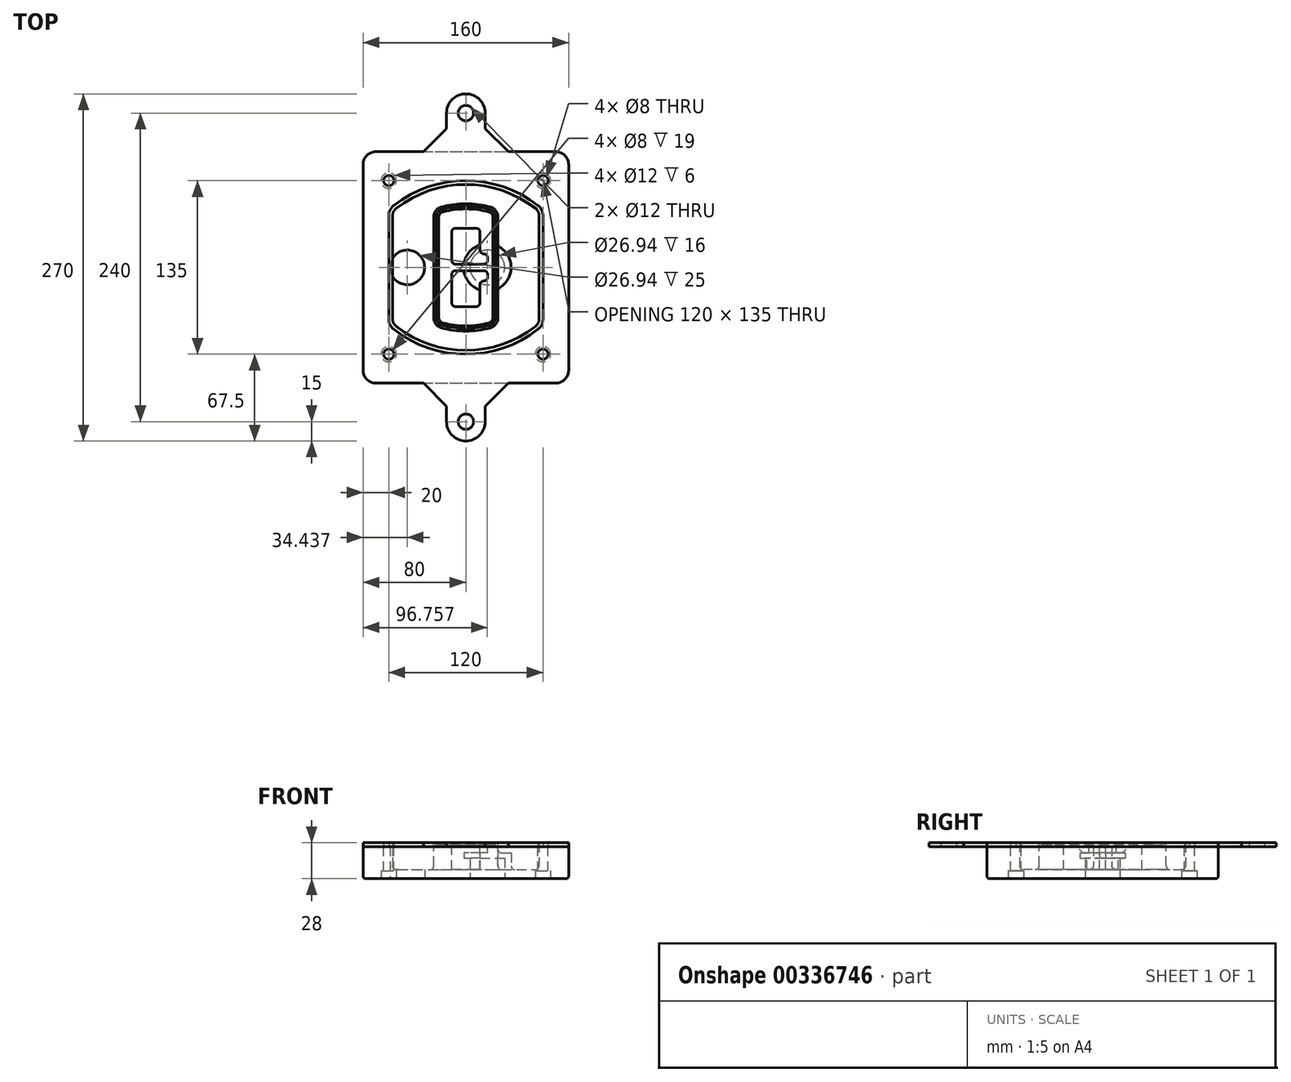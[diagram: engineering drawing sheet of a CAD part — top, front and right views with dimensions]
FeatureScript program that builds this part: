
annotation { "Feature Type Name" : "Feature", "Feature Type Description" : "" }
export const myFeature = defineFeature(function(context is Context, id is Id, definition is map)
    precondition{}
    {
        {
            var Q0;
            Q0=qCreatedBy(makeId("Top.planeOp"),FACE);
            var sketch = newSketch(context, id + "F0", { "sketchPlane" : qUnion([Q0])});
            skPoint(sketch, "E0.rect.middle", {"position": v(0, 0) * mm});
            skLineSegment(sketch, "E1.bottom", {"start": v(-70, -90) * mm, "end": v(70, -90) * mm});
            skLineSegment(sketch, "E1.top", {"start": v(-70, 90) * mm, "end": v(70, 90) * mm});
            skLineSegment(sketch, "E1.left", {"start": v(-80, -80) * mm, "end": v(-80, 80) * mm});
            skLineSegment(sketch, "E1.right", {"start": v(80, -80) * mm, "end": v(80, 80) * mm});
            skLineSegment(sketch, "E2", {"start": v(-80, 90) * mm, "end": v(80, -90) * mm, "construction": true});
            skLineSegment(sketch, "E3", {"start": v(80, 90) * mm, "end": v(-80, -90) * mm, "construction": true});
            skCircle(sketch, "E4", {"center": v(-60, 67.5) * mm, "radius": 4 * mm});
            skCircle(sketch, "E5", {"center": v(60, 67.5) * mm, "radius": 4 * mm});
            skCircle(sketch, "E6", {"center": v(60, -67.5) * mm, "radius": 4 * mm});
            skCircle(sketch, "E7", {"center": v(-60, -67.5) * mm, "radius": 4 * mm});
            skLineSegment(sketch, "E8", {"start": v(-60, 67.5) * mm, "end": v(60, 67.5) * mm, "construction": true});
            skLineSegment(sketch, "E9", {"start": v(60, 67.5) * mm, "end": v(60, -67.5) * mm, "construction": true});
            skLineSegment(sketch, "E10", {"start": v(60, -67.5) * mm, "end": v(-60, -67.5) * mm, "construction": true});
            skLineSegment(sketch, "E11", {"start": v(-60, -67.5) * mm, "end": v(-60, 67.5) * mm, "construction": true});
            skLineSegment(sketch, "E12", {"start": v(-60, 40.3) * mm, "end": v(-60, -40.3) * mm});
            skLineSegment(sketch, "E13", {"start": v(60, 40.3) * mm, "end": v(60, -40.3) * mm});
            skArc(sketch, "E14", {"start": v(56.15, 48.18) * mm, "mid": v(0, 67.5) * mm, "end": v(-56.15, 48.18) * mm});
            skArc(sketch, "E15", {"start": v(-56.15, -48.18) * mm, "mid": v(0, -67.5) * mm, "end": v(56.15, -48.18) * mm});
            skLineSegment(sketch, "E16", {"start": v(-60, 0) * mm, "end": v(60, 0) * mm, "construction": true});
            skPoint(sketch, "E17.visualSharp", {"position": v(-60, -45) * mm});
            skArc(sketch, "E17.filletArc", {"start": v(-60, -40.3) * mm, "mid": v(-58.99, -44.68) * mm, "end": v(-56.15, -48.18) * mm});
            skPoint(sketch, "E18.visualSharp", {"position": v(-60, 45) * mm});
            skArc(sketch, "E18.filletArc", {"start": v(-56.15, 48.18) * mm, "mid": v(-58.99, 44.68) * mm, "end": v(-60, 40.3) * mm});
            skPoint(sketch, "E19.visualSharp", {"position": v(60, 45) * mm});
            skArc(sketch, "E19.filletArc", {"start": v(60, 40.3) * mm, "mid": v(58.99, 44.68) * mm, "end": v(56.15, 48.18) * mm});
            skPoint(sketch, "E20.visualSharp", {"position": v(60, -45) * mm});
            skArc(sketch, "E20.filletArc", {"start": v(56.15, -48.18) * mm, "mid": v(58.99, -44.68) * mm, "end": v(60, -40.3) * mm});
            skPoint(sketch, "E21.visualSharp", {"position": v(-80, 90) * mm});
            skArc(sketch, "E21.filletArc", {"start": v(-70, 90) * mm, "mid": v(-77.07, 87.07) * mm, "end": v(-80, 80) * mm});
            skPoint(sketch, "E22.visualSharp", {"position": v(80, 90) * mm});
            skArc(sketch, "E22.filletArc", {"start": v(80, 80) * mm, "mid": v(77.07, 87.07) * mm, "end": v(70, 90) * mm});
            skPoint(sketch, "E23.visualSharp", {"position": v(80, -90) * mm});
            skArc(sketch, "E23.filletArc", {"start": v(70, -90) * mm, "mid": v(77.07, -87.07) * mm, "end": v(80, -80) * mm});
            skPoint(sketch, "E24.visualSharp", {"position": v(-80, -90) * mm});
            skArc(sketch, "E24.filletArc", {"start": v(-80, -80) * mm, "mid": v(-77.07, -87.07) * mm, "end": v(-70, -90) * mm});
            skArc(sketch, "E25.0", {"start": v(57, 40.3) * mm, "mid": v(56.3, 43.36) * mm, "end": v(54.3, 45.81) * mm});
            skLineSegment(sketch, "E25.1", {"start": v(57, 40.3) * mm, "end": v(57, -40.3) * mm});
            skArc(sketch, "E25.2", {"start": v(54.3, -45.81) * mm, "mid": v(56.3, -43.36) * mm, "end": v(57, -40.3) * mm});
            skArc(sketch, "E25.3", {"start": v(-54.3, -45.81) * mm, "mid": v(0, -64.5) * mm, "end": v(54.3, -45.81) * mm});
            skArc(sketch, "E25.4", {"start": v(-57, -40.3) * mm, "mid": v(-56.3, -43.36) * mm, "end": v(-54.3, -45.81) * mm});
            skArc(sketch, "E25.5", {"start": v(54.3, 45.81) * mm, "mid": v(0, 64.5) * mm, "end": v(-54.3, 45.81) * mm});
            skLineSegment(sketch, "E25.6", {"start": v(-57, 40.3) * mm, "end": v(-57, -40.3) * mm});
            skArc(sketch, "E25.7", {"start": v(-54.3, 45.81) * mm, "mid": v(-56.3, 43.36) * mm, "end": v(-57, 40.3) * mm});
            skArc(sketch, "E26.0", {"start": v(-58.62, 51.33) * mm, "mid": v(-62.58, 46.43) * mm, "end": v(-64, 40.3) * mm});
            skArc(sketch, "E26.1", {"start": v(58.62, 51.33) * mm, "mid": v(0, 71.5) * mm, "end": v(-58.62, 51.33) * mm});
            skArc(sketch, "E26.2", {"start": v(64, 40.3) * mm, "mid": v(62.58, 46.43) * mm, "end": v(58.62, 51.33) * mm});
            skLineSegment(sketch, "E26.3", {"start": v(64, 40.3) * mm, "end": v(64, -40.3) * mm});
            skArc(sketch, "E26.4", {"start": v(58.62, -51.33) * mm, "mid": v(62.58, -46.43) * mm, "end": v(64, -40.3) * mm});
            skLineSegment(sketch, "E26.5", {"start": v(-64, 40.3) * mm, "end": v(-64, -40.3) * mm});
            skArc(sketch, "E26.6", {"start": v(-58.62, -51.33) * mm, "mid": v(0, -71.5) * mm, "end": v(58.62, -51.33) * mm});
            skArc(sketch, "E26.7", {"start": v(-64, -40.3) * mm, "mid": v(-62.58, -46.43) * mm, "end": v(-58.62, -51.33) * mm});
            skSolve(sketch);
        }
        {
            var Q0;
            Q0=makeQuery(id+"F0.imprint","IMPRINT",FACE,{"disambiguationData":[TD([[makeQuery(id+"F0.imprint","IMPRINT",EDGE,{"derivedFrom":sQuery(id+"F0.wireOp",EDGE,"E1.bottom")}),1.0]])]});
            var Q1;
            Q1=makeQuery(id+"F0.imprint","IMPRINT",FACE,{"disambiguationData":[TD([[makeQuery(id+"F0.imprint","IMPRINT",EDGE,{"derivedFrom":sQuery(id+"F0.wireOp",EDGE,"E12")}),1.0]])]});
            var Q2;
            Q2=makeQuery(id+"F0.imprint","IMPRINT",FACE,{"disambiguationData":[TD([[makeQuery(id+"F0.imprint","IMPRINT",EDGE,{"derivedFrom":sQuery(id+"F0.wireOp",EDGE,"E25.0")}),1.0]])]});
            var Q3;
            Q3=makeQuery(id+"F0.imprint","IMPRINT",FACE,{"disambiguationData":[TD([[makeQuery(id+"F0.imprint","IMPRINT",EDGE,{"derivedFrom":sQuery(id+"F0.wireOp",EDGE,"E12")}),-1.0]])]});
            extrude(context, id + "F1", {"entities" : qUnion([Q0, Q1, Q2, Q3]), "oppositeDirection" : true, "depth" : 25 * mm});
        }
        {
            var Q0;
            Q0=makeQuery(id+"F0.imprint","IMPRINT",FACE,{"disambiguationData":[TD([[makeQuery(id+"F0.imprint","IMPRINT",EDGE,{"derivedFrom":sQuery(id+"F0.wireOp",EDGE,"E12")}),1.0]])]});
            extrude(context, id + "F2", {"entities" : qUnion([Q0]), "operationType" : NewBodyOperationType.ADD, "depth" : 3 * mm});
        }
        {
            var Q0;
            Q0=makeQuery(id+"F0.imprint","IMPRINT",FACE,{"disambiguationData":[TD([[makeQuery(id+"F0.imprint","IMPRINT",EDGE,{"derivedFrom":sQuery(id+"F0.wireOp",EDGE,"E25.0")}),1.0]])]});
            extrude(context, id + "F3", {"entities" : qUnion([Q0]), "operationType" : NewBodyOperationType.REMOVE, "oppositeDirection" : true, "depth" : 18 * mm});
        }
        {
            var Q0;
            Q0=makeQuery(id+"F2.opExtrude","CAP_FACE",FACE,{"disambiguationData":[OSD([sQuery(id+"F0.wireOp",EDGE,"E12"),sQuery(id+"F0.wireOp",EDGE,"E13"),sQuery(id+"F0.wireOp",EDGE,"E14"),sQuery(id+"F0.wireOp",EDGE,"E15"),sQuery(id+"F0.wireOp",EDGE,"E17.filletArc"),sQuery(id+"F0.wireOp",EDGE,"E18.filletArc"),sQuery(id+"F0.wireOp",EDGE,"E19.filletArc"),sQuery(id+"F0.wireOp",EDGE,"E20.filletArc"),sQuery(id+"F0.wireOp",EDGE,"E25.0"),sQuery(id+"F0.wireOp",EDGE,"E25.1"),sQuery(id+"F0.wireOp",EDGE,"E25.2"),sQuery(id+"F0.wireOp",EDGE,"E25.3"),sQuery(id+"F0.wireOp",EDGE,"E25.4"),sQuery(id+"F0.wireOp",EDGE,"E25.5"),sQuery(id+"F0.wireOp",EDGE,"E25.6"),sQuery(id+"F0.wireOp",EDGE,"E25.7")])],"isStart":false});
            var sketch = newSketch(context, id + "F4", { "sketchPlane" : qUnion([Q0])});
            skArc(sketch, "E27.0", {"start": v(-19.08, -46.97) * mm, "mid": v(0, -49.5) * mm, "end": v(19.08, -46.97) * mm});
            skArc(sketch, "E28.0", {"start": v(19.08, 46.97) * mm, "mid": v(0, 49.5) * mm, "end": v(-19.08, 46.97) * mm});
            skLineSegment(sketch, "E29", {"start": v(-25, 39.25) * mm, "end": v(-25, -39.25) * mm});
            skLineSegment(sketch, "E30", {"start": v(25, 39.25) * mm, "end": v(25, -39.25) * mm});
            skLineSegment(sketch, "E31", {"start": v(-25, 45.1) * mm, "end": v(25, 45.1) * mm, "construction": true});
            skLineSegment(sketch, "E32", {"start": v(-25, -45.1) * mm, "end": v(25, -45.1) * mm, "construction": true});
            skPoint(sketch, "E33.visualSharp", {"position": v(-25, 45.1) * mm});
            skArc(sketch, "E33.filletArc", {"start": v(-19.08, 46.97) * mm, "mid": v(-23.35, 44.11) * mm, "end": v(-25, 39.25) * mm});
            skPoint(sketch, "E34.visualSharp", {"position": v(25, 45.1) * mm});
            skArc(sketch, "E34.filletArc", {"start": v(25, 39.25) * mm, "mid": v(23.35, 44.11) * mm, "end": v(19.08, 46.97) * mm});
            skPoint(sketch, "E35.visualSharp", {"position": v(25, -45.1) * mm});
            skArc(sketch, "E35.filletArc", {"start": v(19.08, -46.97) * mm, "mid": v(23.35, -44.11) * mm, "end": v(25, -39.25) * mm});
            skPoint(sketch, "E36.visualSharp", {"position": v(-25, -45.1) * mm});
            skArc(sketch, "E36.filletArc", {"start": v(-25, -39.25) * mm, "mid": v(-23.35, -44.11) * mm, "end": v(-19.08, -46.97) * mm});
            skArc(sketch, "E37.0", {"start": v(54.3, 45.81) * mm, "mid": v(0, 64.5) * mm, "end": v(-54.3, 45.81) * mm});
            skArc(sketch, "E37.1", {"start": v(-54.3, 45.81) * mm, "mid": v(-56.3, 43.36) * mm, "end": v(-57, 40.3) * mm});
            skLineSegment(sketch, "E37.2", {"start": v(-57, 40.3) * mm, "end": v(-57, -40.3) * mm});
            skArc(sketch, "E37.3", {"start": v(-57, -40.3) * mm, "mid": v(-56.3, -43.36) * mm, "end": v(-54.3, -45.81) * mm});
            skArc(sketch, "E37.4", {"start": v(-54.3, -45.81) * mm, "mid": v(0, -64.5) * mm, "end": v(54.3, -45.81) * mm});
            skArc(sketch, "E37.5", {"start": v(54.3, -45.81) * mm, "mid": v(56.3, -43.36) * mm, "end": v(57, -40.3) * mm});
            skLineSegment(sketch, "E37.6", {"start": v(57, 40.3) * mm, "end": v(57, -40.3) * mm});
            skArc(sketch, "E37.7", {"start": v(57, 40.3) * mm, "mid": v(56.3, 43.36) * mm, "end": v(54.3, 45.81) * mm});
            skLineSegment(sketch, "E38.0", {"start": v(23, 39.25) * mm, "end": v(23, -39.25) * mm});
            skArc(sketch, "E38.1", {"start": v(18.56, -45.04) * mm, "mid": v(21.76, -42.9) * mm, "end": v(23, -39.25) * mm});
            skArc(sketch, "E38.2", {"start": v(-18.56, -45.04) * mm, "mid": v(0, -47.5) * mm, "end": v(18.56, -45.04) * mm});
            skArc(sketch, "E38.3", {"start": v(-23, -39.25) * mm, "mid": v(-21.76, -42.9) * mm, "end": v(-18.56, -45.04) * mm});
            skLineSegment(sketch, "E38.4", {"start": v(-23, 39.25) * mm, "end": v(-23, -39.25) * mm});
            skArc(sketch, "E38.5", {"start": v(23, 39.25) * mm, "mid": v(21.76, 42.9) * mm, "end": v(18.56, 45.04) * mm});
            skArc(sketch, "E38.6", {"start": v(-18.56, 45.04) * mm, "mid": v(-21.76, 42.9) * mm, "end": v(-23, 39.25) * mm});
            skArc(sketch, "E38.7", {"start": v(18.56, 45.04) * mm, "mid": v(0, 47.5) * mm, "end": v(-18.56, 45.04) * mm});
            skArc(sketch, "E39.0", {"start": v(21, 39.25) * mm, "mid": v(20.18, 41.68) * mm, "end": v(18.04, 43.1) * mm});
            skLineSegment(sketch, "E39.1", {"start": v(21, 39.25) * mm, "end": v(21, -39.25) * mm});
            skArc(sketch, "E39.2", {"start": v(18.04, -43.1) * mm, "mid": v(20.18, -41.68) * mm, "end": v(21, -39.25) * mm});
            skArc(sketch, "E39.3", {"start": v(-18.04, -43.1) * mm, "mid": v(0, -45.5) * mm, "end": v(18.04, -43.1) * mm});
            skArc(sketch, "E39.4", {"start": v(-21, -39.25) * mm, "mid": v(-20.18, -41.68) * mm, "end": v(-18.04, -43.1) * mm});
            skArc(sketch, "E39.5", {"start": v(18.04, 43.1) * mm, "mid": v(0, 45.5) * mm, "end": v(-18.04, 43.1) * mm});
            skLineSegment(sketch, "E39.6", {"start": v(-21, 39.25) * mm, "end": v(-21, -39.25) * mm});
            skArc(sketch, "E39.7", {"start": v(-18.04, 43.1) * mm, "mid": v(-20.18, 41.68) * mm, "end": v(-21, 39.25) * mm});
            skLineSegment(sketch, "E40", {"start": v(-25, 0) * mm, "end": v(25, 0) * mm, "construction": true});
            skLineSegment(sketch, "E41", {"start": v(-11, 5.5) * mm, "end": v(-11, 27.5) * mm});
            skLineSegment(sketch, "E42", {"start": v(-8, 30.5) * mm, "end": v(8, 30.5) * mm});
            skLineSegment(sketch, "E43", {"start": v(11, 27.5) * mm, "end": v(11, 13.5) * mm});
            skLineSegment(sketch, "E44", {"start": v(14, 10.5) * mm, "end": v(14, 10.5) * mm});
            skLineSegment(sketch, "E45", {"start": v(17, 7.5) * mm, "end": v(17, 5.5) * mm});
            skLineSegment(sketch, "E46", {"start": v(14, 2.5) * mm, "end": v(-8, 2.5) * mm});
            skPoint(sketch, "E47.visualSharp", {"position": v(-11, 30.5) * mm});
            skArc(sketch, "E47.filletArc", {"start": v(-8, 30.5) * mm, "mid": v(-10.12, 29.62) * mm, "end": v(-11, 27.5) * mm});
            skPoint(sketch, "E48.visualSharp", {"position": v(11, 30.5) * mm});
            skArc(sketch, "E48.filletArc", {"start": v(11, 27.5) * mm, "mid": v(10.12, 29.62) * mm, "end": v(8, 30.5) * mm});
            skPoint(sketch, "E49.visualSharp", {"position": v(11, 10.5) * mm});
            skArc(sketch, "E49.filletArc", {"start": v(11, 13.5) * mm, "mid": v(11.88, 11.38) * mm, "end": v(14, 10.5) * mm});
            skPoint(sketch, "E50.visualSharp", {"position": v(17, 10.5) * mm});
            skArc(sketch, "E50.filletArc", {"start": v(17, 7.5) * mm, "mid": v(16.12, 9.62) * mm, "end": v(14, 10.5) * mm});
            skPoint(sketch, "E51.visualSharp", {"position": v(17, 2.5) * mm});
            skArc(sketch, "E51.filletArc", {"start": v(14, 2.5) * mm, "mid": v(16.12, 3.38) * mm, "end": v(17, 5.5) * mm});
            skPoint(sketch, "E52.visualSharp", {"position": v(-11, 2.5) * mm});
            skArc(sketch, "E52.filletArc", {"start": v(-11, 5.5) * mm, "mid": v(-10.12, 3.38) * mm, "end": v(-8, 2.5) * mm});
            skLineSegment(sketch, "E53.0.MirrorCS", {"start": v(14, -2.5) * mm, "end": v(-8, -2.5) * mm});
            skArc(sketch, "E54.0.MirrorCS", {"start": v(-11, -5.5) * mm, "mid": v(-10.12, -3.38) * mm, "end": v(-8, -2.5) * mm});
            skLineSegment(sketch, "E55.0.MirrorCS", {"start": v(-11, -5.5) * mm, "end": v(-11, -27.5) * mm});
            skArc(sketch, "E56.0.MirrorCS", {"start": v(-8, -30.5) * mm, "mid": v(-10.12, -29.62) * mm, "end": v(-11, -27.5) * mm});
            skLineSegment(sketch, "E57.0.MirrorCS", {"start": v(-8, -30.5) * mm, "end": v(8, -30.5) * mm});
            skArc(sketch, "E58.0.MirrorCS", {"start": v(11, -27.5) * mm, "mid": v(10.12, -29.62) * mm, "end": v(8, -30.5) * mm});
            skLineSegment(sketch, "E59.0.MirrorCS", {"start": v(11, -27.5) * mm, "end": v(11, -13.5) * mm});
            skArc(sketch, "E60.0.MirrorCS", {"start": v(11, -13.5) * mm, "mid": v(11.88, -11.38) * mm, "end": v(14, -10.5) * mm});
            skArc(sketch, "E61.0.MirrorCS", {"start": v(17, -7.5) * mm, "mid": v(16.12, -9.62) * mm, "end": v(14, -10.5) * mm});
            skLineSegment(sketch, "E62.0.MirrorCS", {"start": v(17, -7.5) * mm, "end": v(17, -5.5) * mm});
            skArc(sketch, "E63.0.MirrorCS", {"start": v(14, -2.5) * mm, "mid": v(16.12, -3.38) * mm, "end": v(17, -5.5) * mm});
            skSolve(sketch);
        }
        {
            var Q0;
            Q0=makeQuery(id+"F4.imprint","IMPRINT",FACE,{"disambiguationData":[TD([[makeQuery(id+"F4.imprint","IMPRINT",EDGE,{"derivedFrom":sQuery(id+"F4.wireOp",EDGE,"E27.0")}),1.0]])]});
            var Q1;
            Q1=makeQuery(id+"F4.imprint","IMPRINT",FACE,{"disambiguationData":[TD([[makeQuery(id+"F4.imprint","IMPRINT",EDGE,{"derivedFrom":sQuery(id+"F4.wireOp",EDGE,"E38.0")}),-1.0]])]});
            var Q2;
            Q2=makeQuery(id+"F4.imprint","IMPRINT",FACE,{"disambiguationData":[TD([[makeQuery(id+"F4.imprint","IMPRINT",EDGE,{"derivedFrom":sQuery(id+"F4.wireOp",EDGE,"E39.0")}),1.0]])]});
            extrude(context, id + "F5", {"entities" : qUnion([Q0, Q1, Q2]), "operationType" : NewBodyOperationType.ADD, "endBound" : BoundingType.UP_TO_NEXT, "oppositeDirection" : true, "depth" : 25 * mm});
        }
        {
            var Q0;
            Q0=makeQuery(id+"F4.imprint","IMPRINT",FACE,{"disambiguationData":[TD([[makeQuery(id+"F4.imprint","IMPRINT",EDGE,{"derivedFrom":sQuery(id+"F4.wireOp",EDGE,"E38.0")}),-1.0]])]});
            extrude(context, id + "F6", {"entities" : qUnion([Q0]), "operationType" : NewBodyOperationType.REMOVE, "oppositeDirection" : true, "depth" : 2 * mm});
        }
        {
            var Q0;
            Q0=makeQuery(id+"F1.opExtrude","CAP_FACE",FACE,{"disambiguationData":[OSD([sQuery(id+"F0.wireOp",EDGE,"E1.bottom"),sQuery(id+"F0.wireOp",EDGE,"E1.top"),sQuery(id+"F0.wireOp",EDGE,"E1.left"),sQuery(id+"F0.wireOp",EDGE,"E1.right"),sQuery(id+"F0.wireOp",EDGE,"E4"),sQuery(id+"F0.wireOp",EDGE,"E5"),sQuery(id+"F0.wireOp",EDGE,"E6"),sQuery(id+"F0.wireOp",EDGE,"E7"),sQuery(id+"F0.wireOp",EDGE,"E21.filletArc"),sQuery(id+"F0.wireOp",EDGE,"E22.filletArc"),sQuery(id+"F0.wireOp",EDGE,"E23.filletArc"),sQuery(id+"F0.wireOp",EDGE,"E24.filletArc")])],"isStart":false});
            var sketch = newSketch(context, id + "F7", { "sketchPlane" : qUnion([Q0])});
            skCircle(sketch, "E64", {"center": v(16.76, 0) * mm, "radius": 13.47 * mm});
            skCircle(sketch, "E65", {"center": v(-45.56, 0) * mm, "radius": 13.47 * mm});
            skLineSegment(sketch, "E66", {"start": v(80, 0) * mm, "end": v(-80, 0) * mm});
            skCircle(sketch, "E67", {"center": v(16.76, 0) * mm, "radius": 18.47 * mm});
            skCircle(sketch, "E68", {"center": v(60, -67.5) * mm, "radius": 6 * mm});
            skCircle(sketch, "E69", {"center": v(-60, -67.5) * mm, "radius": 6 * mm});
            skCircle(sketch, "E70", {"center": v(-60, 67.5) * mm, "radius": 6 * mm});
            skCircle(sketch, "E71", {"center": v(60, 67.5) * mm, "radius": 6 * mm});
            skSolve(sketch);
        }
        {
            var Q0;
            {var subQ1=sQuery(id+"F7.wireOp",EDGE,"E66");var subQ4=sQuery(id+"F7.wireOp",EDGE,"E64");var subQ6=makeQuery(id+"F7.imprint","INTERSECT",VERTEX,{"disambiguationData":[OD(0.0)],"derivedFrom":[subQ4,subQ1]});Q0=makeQuery(id+"F7.imprint","IMPRINT",FACE,{"disambiguationData":[TD([[makeQuery(id+"F7.imprint","IMPRINT",EDGE,{"disambiguationData":[TD([[subQ6,-1.0]])],"derivedFrom":subQ4}),-1.0]])]});}
            var Q1;
            {var subQ0=sQuery(id+"F7.wireOp",EDGE,"E66");var subQ1=sQuery(id+"F7.wireOp",EDGE,"E64");var subQ3=makeQuery(id+"F7.imprint","INTERSECT",VERTEX,{"disambiguationData":[OD(0.0)],"derivedFrom":[subQ1,subQ0]});Q1=makeQuery(id+"F7.imprint","IMPRINT",FACE,{"disambiguationData":[TD([[makeQuery(id+"F7.imprint","IMPRINT",EDGE,{"disambiguationData":[TD([[subQ3,-1.0]])],"derivedFrom":subQ1}),1.0]])]});}
            var Q2;
            {var subQ0=sQuery(id+"F7.wireOp",EDGE,"E66");var subQ1=sQuery(id+"F7.wireOp",EDGE,"E64");var subQ3=makeQuery(id+"F7.imprint","INTERSECT",VERTEX,{"disambiguationData":[OD(0.0)],"derivedFrom":[subQ1,subQ0]});Q2=makeQuery(id+"F7.imprint","IMPRINT",FACE,{"disambiguationData":[TD([[makeQuery(id+"F7.imprint","IMPRINT",EDGE,{"disambiguationData":[TD([[subQ3,1.0]])],"derivedFrom":subQ1}),1.0]])]});}
            var Q3;
            {var subQ1=sQuery(id+"F7.wireOp",EDGE,"E66");var subQ4=sQuery(id+"F7.wireOp",EDGE,"E64");var subQ6=makeQuery(id+"F7.imprint","INTERSECT",VERTEX,{"disambiguationData":[OD(0.0)],"derivedFrom":[subQ4,subQ1]});Q3=makeQuery(id+"F7.imprint","IMPRINT",FACE,{"disambiguationData":[TD([[makeQuery(id+"F7.imprint","IMPRINT",EDGE,{"disambiguationData":[TD([[subQ6,1.0]])],"derivedFrom":subQ4}),-1.0]])]});}
            extrude(context, id + "F8", {"entities" : qUnion([Q0, Q1, Q2, Q3]), "operationType" : NewBodyOperationType.ADD, "oppositeDirection" : true, "depth" : 20 * mm});
        }
        {
            var Q0;
            {var subQ0=sQuery(id+"F7.wireOp",EDGE,"E66");var subQ1=sQuery(id+"F7.wireOp",EDGE,"E64");var subQ3=makeQuery(id+"F7.imprint","INTERSECT",VERTEX,{"disambiguationData":[OD(0.0)],"derivedFrom":[subQ1,subQ0]});Q0=makeQuery(id+"F7.imprint","IMPRINT",FACE,{"disambiguationData":[TD([[makeQuery(id+"F7.imprint","IMPRINT",EDGE,{"disambiguationData":[TD([[subQ3,-1.0]])],"derivedFrom":subQ1}),1.0]])]});}
            var Q1;
            {var subQ0=sQuery(id+"F7.wireOp",EDGE,"E66");var subQ1=sQuery(id+"F7.wireOp",EDGE,"E64");var subQ3=makeQuery(id+"F7.imprint","INTERSECT",VERTEX,{"disambiguationData":[OD(0.0)],"derivedFrom":[subQ1,subQ0]});Q1=makeQuery(id+"F7.imprint","IMPRINT",FACE,{"disambiguationData":[TD([[makeQuery(id+"F7.imprint","IMPRINT",EDGE,{"disambiguationData":[TD([[subQ3,1.0]])],"derivedFrom":subQ1}),1.0]])]});}
            extrude(context, id + "F9", {"entities" : qUnion([Q0, Q1]), "operationType" : NewBodyOperationType.REMOVE, "oppositeDirection" : true, "depth" : 16 * mm});
        }
        {
            var Q0;
            {var subQ0=sQuery(id+"F7.wireOp",EDGE,"E66");var subQ1=sQuery(id+"F7.wireOp",EDGE,"E65");var subQ3=makeQuery(id+"F7.imprint","INTERSECT",VERTEX,{"disambiguationData":[OD(0.0)],"derivedFrom":[subQ1,subQ0]});Q0=makeQuery(id+"F7.imprint","IMPRINT",FACE,{"disambiguationData":[TD([[makeQuery(id+"F7.imprint","IMPRINT",EDGE,{"disambiguationData":[TD([[subQ3,-1.0]])],"derivedFrom":subQ1}),1.0]])]});}
            var Q1;
            {var subQ0=sQuery(id+"F7.wireOp",EDGE,"E66");var subQ1=sQuery(id+"F7.wireOp",EDGE,"E65");var subQ3=makeQuery(id+"F7.imprint","INTERSECT",VERTEX,{"disambiguationData":[OD(0.0)],"derivedFrom":[subQ1,subQ0]});Q1=makeQuery(id+"F7.imprint","IMPRINT",FACE,{"disambiguationData":[TD([[makeQuery(id+"F7.imprint","IMPRINT",EDGE,{"disambiguationData":[TD([[subQ3,1.0]])],"derivedFrom":subQ1}),1.0]])]});}
            extrude(context, id + "F10", {"entities" : qUnion([Q0, Q1]), "operationType" : NewBodyOperationType.REMOVE, "oppositeDirection" : true, "depth" : 25 * mm});
        }
        {
            var Q0;
            Q0=makeQuery(id+"F7.imprint","IMPRINT",FACE,{"disambiguationData":[TD([[makeQuery(id+"F7.imprint","IMPRINT",EDGE,{"derivedFrom":sQuery(id+"F7.wireOp",EDGE,"E68")}),1.0]])]});
            var Q1;
            Q1=makeQuery(id+"F7.imprint","IMPRINT",FACE,{"disambiguationData":[TD([[makeQuery(id+"F7.imprint","IMPRINT",EDGE,{"derivedFrom":makeQuery(id+"F1.opExtrude","CAP_EDGE",EDGE,{"disambiguationData":[OSD([sQuery(id+"F0.wireOp",EDGE,"E5")])],"isStart":false})}),-1.0]])]});
            var Q2;
            Q2=makeQuery(id+"F7.imprint","IMPRINT",FACE,{"disambiguationData":[TD([[makeQuery(id+"F7.imprint","IMPRINT",EDGE,{"derivedFrom":sQuery(id+"F7.wireOp",EDGE,"E69")}),1.0]])]});
            var Q3;
            Q3=makeQuery(id+"F7.imprint","IMPRINT",FACE,{"disambiguationData":[TD([[makeQuery(id+"F7.imprint","IMPRINT",EDGE,{"derivedFrom":makeQuery(id+"F1.opExtrude","CAP_EDGE",EDGE,{"disambiguationData":[OSD([sQuery(id+"F0.wireOp",EDGE,"E4")])],"isStart":false})}),-1.0]])]});
            var Q4;
            Q4=makeQuery(id+"F7.imprint","IMPRINT",FACE,{"disambiguationData":[TD([[makeQuery(id+"F7.imprint","IMPRINT",EDGE,{"derivedFrom":sQuery(id+"F7.wireOp",EDGE,"E70")}),1.0]])]});
            var Q5;
            Q5=makeQuery(id+"F7.imprint","IMPRINT",FACE,{"disambiguationData":[TD([[makeQuery(id+"F7.imprint","IMPRINT",EDGE,{"derivedFrom":makeQuery(id+"F1.opExtrude","CAP_EDGE",EDGE,{"disambiguationData":[OSD([sQuery(id+"F0.wireOp",EDGE,"E7")])],"isStart":false})}),-1.0]])]});
            var Q6;
            Q6=makeQuery(id+"F7.imprint","IMPRINT",FACE,{"disambiguationData":[TD([[makeQuery(id+"F7.imprint","IMPRINT",EDGE,{"derivedFrom":sQuery(id+"F7.wireOp",EDGE,"E71")}),1.0]])]});
            var Q7;
            Q7=makeQuery(id+"F7.imprint","IMPRINT",FACE,{"disambiguationData":[TD([[makeQuery(id+"F7.imprint","IMPRINT",EDGE,{"derivedFrom":makeQuery(id+"F1.opExtrude","CAP_EDGE",EDGE,{"disambiguationData":[OSD([sQuery(id+"F0.wireOp",EDGE,"E6")])],"isStart":false})}),-1.0]])]});
            extrude(context, id + "F11", {"entities" : qUnion([Q0, Q1, Q2, Q3, Q4, Q5, Q6, Q7]), "operationType" : NewBodyOperationType.REMOVE, "oppositeDirection" : true, "depth" : 6 * mm});
        }
        {
            var Q0;
            Q0=makeQuery(id+"F9.boolean.opBoolean","COPY",FACE,{"derivedFrom":makeQuery(id+"F9.opExtrude","CAP_FACE",FACE,{"disambiguationData":[OSD([sQuery(id+"F7.wireOp",EDGE,"E64")])],"isStart":false})});
            var sketch = newSketch(context, id + "F12", { "sketchPlane" : qUnion([Q0])});
            skArc(sketch, "E72.0", {"start": v(11, 17.55) * mm, "mid": v(2.57, 11.82) * mm, "end": v(-1.54, 2.5) * mm});
            skArc(sketch, "E72.1", {"start": v(-1.54, -2.5) * mm, "mid": v(2.57, -11.82) * mm, "end": v(11, -17.55) * mm});
            skLineSegment(sketch, "E73", {"start": v(-1.54, -2.5) * mm, "end": v(14, -2.5) * mm});
            skLineSegment(sketch, "E74.0", {"start": v(14, 2.5) * mm, "end": v(-1.54, 2.5) * mm});
            skArc(sketch, "E74.1", {"start": v(14, 2.5) * mm, "mid": v(16.12, 3.38) * mm, "end": v(17, 5.5) * mm});
            skLineSegment(sketch, "E74.2", {"start": v(17, 7.5) * mm, "end": v(17, 5.5) * mm});
            skArc(sketch, "E74.3", {"start": v(17, 7.5) * mm, "mid": v(16.12, 9.62) * mm, "end": v(14, 10.5) * mm});
            skArc(sketch, "E74.4", {"start": v(11, 13.5) * mm, "mid": v(11.88, 11.38) * mm, "end": v(14, 10.5) * mm});
            skLineSegment(sketch, "E74.5", {"start": v(11, 17.55) * mm, "end": v(11, 13.5) * mm});
            skLineSegment(sketch, "E74.7", {"start": v(14, -2.5) * mm, "end": v(-1.54, -2.5) * mm});
            skArc(sketch, "E74.8", {"start": v(14, -2.5) * mm, "mid": v(16.12, -3.38) * mm, "end": v(17, -5.5) * mm});
            skLineSegment(sketch, "E74.9", {"start": v(17, -7.5) * mm, "end": v(17, -5.5) * mm});
            skArc(sketch, "E74.10", {"start": v(17, -7.5) * mm, "mid": v(16.12, -9.62) * mm, "end": v(14, -10.5) * mm});
            skArc(sketch, "E74.11", {"start": v(11, -13.5) * mm, "mid": v(11.88, -11.38) * mm, "end": v(14, -10.5) * mm});
            skLineSegment(sketch, "E74.12", {"start": v(11, -17.55) * mm, "end": v(11, -13.5) * mm});
            skPoint(sketch, "E75.orphan", {"position": v(11, -27.5) * mm});
            skPoint(sketch, "E76.orphan", {"position": v(-8, -2.5) * mm});
            skPoint(sketch, "E77.orphan", {"position": v(-8, 2.5) * mm});
            skPoint(sketch, "E78.orphan", {"position": v(11, 27.5) * mm});
            skSolve(sketch);
        }
        {
            var Q0;
            {var subQ7=sQuery(id+"F12.wireOp",EDGE,"E72.0");var subQ14=sQuery(id+"F12.wireOp",EDGE,"E72.1");var subQ16=sQuery(id+"F12.wireOp",EDGE,"E74.1");var subQ18=sQuery(id+"F12.wireOp",EDGE,"E74.8");Q0=qUnion([makeQuery(id+"F12.imprint","IMPRINT",FACE,{"disambiguationData":[TD([[makeQuery(id+"F12.imprint","IMPRINT",EDGE,{"derivedFrom":subQ7}),1.0]])]}),makeQuery(id+"F12.imprint","IMPRINT",FACE,{"disambiguationData":[TD([[makeQuery(id+"F12.imprint","IMPRINT",EDGE,{"derivedFrom":subQ14}),1.0]])]}),makeQuery(id+"F12.imprint","IMPRINT",FACE,{"disambiguationData":[TD([[makeQuery(id+"F12.imprint","IMPRINT",EDGE,{"derivedFrom":subQ16}),1.0]])]}),makeQuery(id+"F12.imprint","IMPRINT",FACE,{"disambiguationData":[TD([[makeQuery(id+"F12.imprint","IMPRINT",EDGE,{"derivedFrom":subQ18}),-1.0]])]})]);}
            var Q1;
            Q1=makeQuery(id+"F5.boolean.opBoolean","SPLIT",FACE,{"disambiguationData":[TD([makeQuery(id+"F5.opExtrude","SWEPT_FACE",FACE,{"disambiguationData":[OSD([sQuery(id+"F4.wireOp",EDGE,"E41")])]})])],"derivedFrom":makeQuery(id+"F3.boolean.opBoolean","COPY",FACE,{"derivedFrom":makeQuery(id+"F3.opExtrude","CAP_FACE",FACE,{"disambiguationData":[OSD([sQuery(id+"F0.wireOp",EDGE,"E25.0"),sQuery(id+"F0.wireOp",EDGE,"E25.1"),sQuery(id+"F0.wireOp",EDGE,"E25.2"),sQuery(id+"F0.wireOp",EDGE,"E25.3"),sQuery(id+"F0.wireOp",EDGE,"E25.4"),sQuery(id+"F0.wireOp",EDGE,"E25.5"),sQuery(id+"F0.wireOp",EDGE,"E25.6"),sQuery(id+"F0.wireOp",EDGE,"E25.7")])],"isStart":false})})});
            extrude(context, id + "F13", {"entities" : qUnion([Q0]), "operationType" : NewBodyOperationType.REMOVE, "endBound" : BoundingType.UP_TO_SURFACE, "endBoundEntityFace" : qUnion([Q1]), "depth" : 25 * mm});
        }
        {
            var Q0;
            Q0=makeQuery(id+"F3.boolean.opBoolean","COPY",EDGE,{"derivedFrom":makeQuery(id+"F3.opExtrude","CAP_EDGE",EDGE,{"disambiguationData":[OSD([sQuery(id+"F0.wireOp",EDGE,"E25.6")])],"isStart":false})});
            var Q1;
            Q1=makeQuery(id+"F8.boolean.opBoolean","INTERSECT",EDGE,{"derivedFrom":[makeQuery(id+"F5.opExtrude","SWEPT_FACE",FACE,{"disambiguationData":[OSD([sQuery(id+"F4.wireOp",EDGE,"E30")])]}),makeQuery(id+"F8.opExtrude","CAP_FACE",FACE,{"disambiguationData":[OSD([sQuery(id+"F7.wireOp",EDGE,"E67")])],"isStart":false})]});
            var Q2;
            Q2=makeQuery(id+"F8.boolean.opBoolean","INTERSECT",EDGE,{"disambiguationData":[OD(1.0)],"derivedFrom":[makeQuery(id+"F5.opExtrude","SWEPT_FACE",FACE,{"disambiguationData":[OSD([sQuery(id+"F4.wireOp",EDGE,"E30")])]}),makeQuery(id+"F8.opExtrude","SWEPT_FACE",FACE,{"disambiguationData":[OSD([sQuery(id+"F7.wireOp",EDGE,"E67")])]})]});
            var Q3;
            {var subQ0=sQuery(id+"F4.wireOp",EDGE,"E30");Q3=makeQuery(id+"F8.boolean.opBoolean","SPLIT",EDGE,{"disambiguationData":[TD([makeQuery(id+"F5.opExtrude","SWEPT_FACE",FACE,{"disambiguationData":[OSD([sQuery(id+"F4.wireOp",EDGE,"E35.filletArc")])]})])],"derivedFrom":makeQuery(id+"F5.opExtrude","CAP_EDGE",EDGE,{"disambiguationData":[OSD([subQ0])],"isStart":false})});}
            var Q4;
            {var subQ0=sQuery(id+"F0.wireOp",EDGE,"E25.7");var subQ1=sQuery(id+"F0.wireOp",EDGE,"E25.1");var subQ2=sQuery(id+"F0.wireOp",EDGE,"E25.6");var subQ3=sQuery(id+"F0.wireOp",EDGE,"E25.5");var subQ4=sQuery(id+"F0.wireOp",EDGE,"E25.4");var subQ5=sQuery(id+"F0.wireOp",EDGE,"E25.0");var subQ6=sQuery(id+"F0.wireOp",EDGE,"E25.2");var subQ7=sQuery(id+"F0.wireOp",EDGE,"E25.3");Q4=makeQuery(id+"F8.boolean.opBoolean","INTERSECT",EDGE,{"derivedFrom":[makeQuery(id+"F5.boolean.opBoolean","SPLIT",FACE,{"disambiguationData":[TD([makeQuery(id+"F2.opExtrude","SWEPT_FACE",FACE,{"disambiguationData":[OSD([subQ5])]})])],"derivedFrom":makeQuery(id+"F3.boolean.opBoolean","COPY",FACE,{"derivedFrom":makeQuery(id+"F3.opExtrude","CAP_FACE",FACE,{"disambiguationData":[OSD([subQ5,subQ1,subQ6,subQ7,subQ4,subQ3,subQ2,subQ0])],"isStart":false})})}),makeQuery(id+"F8.opExtrude","SWEPT_FACE",FACE,{"disambiguationData":[OSD([sQuery(id+"F7.wireOp",EDGE,"E67")])]})]});}
            var Q5;
            Q5=makeQuery(id+"F8.boolean.opBoolean","INTERSECT",EDGE,{"disambiguationData":[OD(0.0)],"derivedFrom":[makeQuery(id+"F5.opExtrude","SWEPT_FACE",FACE,{"disambiguationData":[OSD([sQuery(id+"F4.wireOp",EDGE,"E30")])]}),makeQuery(id+"F8.opExtrude","SWEPT_FACE",FACE,{"disambiguationData":[OSD([sQuery(id+"F7.wireOp",EDGE,"E67")])]})]});
            fillet(context, id + "F14", {"entities" : qUnion([Q0, Q1, Q2, Q3, Q4, Q5]), "radius" : 3 * mm, "tangentPropagation" : true, "allowEdgeOverflow" : false});
        }
        {
            var Q0;
            Q0=makeQuery(id+"F1.opExtrude","CAP_EDGE",EDGE,{"disambiguationData":[OSD([sQuery(id+"F0.wireOp",EDGE,"E1.bottom")])],"isStart":false});
            fillet(context, id + "F15", {"entities" : qUnion([Q0]), "radius" : 2 * mm, "tangentPropagation" : true, "allowEdgeOverflow" : false});
        }
        {
            var Q0;
            {var subQ0=sQuery(id+"F0.wireOp",EDGE,"E21.filletArc");var subQ1=sQuery(id+"F0.wireOp",EDGE,"E7");var subQ2=sQuery(id+"F0.wireOp",EDGE,"E6");var subQ3=sQuery(id+"F0.wireOp",EDGE,"E5");var subQ4=sQuery(id+"F0.wireOp",EDGE,"E4");var subQ5=sQuery(id+"F0.wireOp",EDGE,"E22.filletArc");var subQ6=sQuery(id+"F0.wireOp",EDGE,"E1.bottom");var subQ7=sQuery(id+"F0.wireOp",EDGE,"E1.right");var subQ8=sQuery(id+"F0.wireOp",EDGE,"E1.top");var subQ9=sQuery(id+"F0.wireOp",EDGE,"E1.left");var subQ10=sQuery(id+"F0.wireOp",EDGE,"E23.filletArc");var subQ11=sQuery(id+"F0.wireOp",EDGE,"E24.filletArc");Q0=makeQuery(id+"F2.boolean.opBoolean","SPLIT",FACE,{"disambiguationData":[TD([makeQuery(id+"F1.opExtrude","SWEPT_FACE",FACE,{"disambiguationData":[OSD([subQ6])]})])],"derivedFrom":makeQuery(id+"F1.opExtrude","CAP_FACE",FACE,{"disambiguationData":[OSD([subQ6,subQ8,subQ9,subQ7,subQ4,subQ3,subQ2,subQ1,subQ0,subQ5,subQ10,subQ11])],"isStart":true})});}
            var sketch = newSketch(context, id + "F16", { "sketchPlane" : qUnion([Q0])});
            skLineSegment(sketch, "E79", {"start": v(0, 90) * mm, "end": v(0, 120) * mm, "construction": true});
            skPoint(sketch, "E79.endSnap0", {"position": v(0, 90) * mm});
            skCircle(sketch, "E80", {"center": v(0, 120) * mm, "radius": 6 * mm});
            skLineSegment(sketch, "E81", {"start": v(15, 108) * mm, "end": v(33, 90) * mm});
            skLineSegment(sketch, "E82", {"start": v(-15, 108) * mm, "end": v(-33, 90) * mm});
            skLineSegment(sketch, "E83", {"start": v(-15, 108) * mm, "end": v(-15, 120) * mm});
            skLineSegment(sketch, "E84", {"start": v(15, 108) * mm, "end": v(15, 120) * mm});
            skArc(sketch, "E85", {"start": v(15, 120) * mm, "mid": v(0, 135) * mm, "end": v(-15, 120) * mm});
            skLineSegment(sketch, "E86", {"start": v(0, -90) * mm, "end": v(0, -120) * mm, "construction": true});
            skCircle(sketch, "E87", {"center": v(0, -120) * mm, "radius": 6 * mm});
            skLineSegment(sketch, "E88", {"start": v(15, -108) * mm, "end": v(33, -90) * mm});
            skLineSegment(sketch, "E89", {"start": v(-15, -108) * mm, "end": v(-33, -90) * mm});
            skLineSegment(sketch, "E90", {"start": v(-15, -108) * mm, "end": v(-15, -120) * mm});
            skLineSegment(sketch, "E91", {"start": v(15, -120) * mm, "end": v(15, -108) * mm});
            skArc(sketch, "E92", {"start": v(-15, -120) * mm, "mid": v(0, -135) * mm, "end": v(15, -120) * mm});
            skSolve(sketch);
        }
        {
            var Q0;
            Q0=makeQuery(id+"F16.imprint","IMPRINT",FACE,{"disambiguationData":[TD([[makeQuery(id+"F16.imprint","IMPRINT",EDGE,{"derivedFrom":makeQuery(id+"F1.opExtrude","CAP_EDGE",EDGE,{"disambiguationData":[OSD([sQuery(id+"F0.wireOp",EDGE,"E1.left")])],"isStart":true})}),-1.0]])]});
            var Q1;
            Q1=makeQuery(id+"F16.imprint","IMPRINT",FACE,{"disambiguationData":[TD([[makeQuery(id+"F16.imprint","IMPRINT",EDGE,{"derivedFrom":sQuery(id+"F16.wireOp",EDGE,"E80")}),-1.0]])]});
            var Q2;
            Q2=makeQuery(id+"F16.imprint","IMPRINT",FACE,{"disambiguationData":[TD([[makeQuery(id+"F16.imprint","IMPRINT",EDGE,{"derivedFrom":sQuery(id+"F16.wireOp",EDGE,"E87")}),-1.0]])]});
            var Q3;
            {var subQ0=sQuery(id+"F4.wireOp",EDGE,"E36.filletArc");var subQ1=sQuery(id+"F4.wireOp",EDGE,"E35.filletArc");var subQ2=sQuery(id+"F4.wireOp",EDGE,"E34.filletArc");var subQ3=sQuery(id+"F4.wireOp",EDGE,"E33.filletArc");var subQ4=sQuery(id+"F4.wireOp",EDGE,"E27.0");var subQ5=sQuery(id+"F4.wireOp",EDGE,"E30");var subQ6=sQuery(id+"F4.wireOp",EDGE,"E28.0");var subQ7=sQuery(id+"F4.wireOp",EDGE,"E29");Q3=makeQuery(id+"F6.boolean.opBoolean","SPLIT",FACE,{"disambiguationData":[TD([makeQuery(id+"F5.opExtrude","SWEPT_FACE",FACE,{"disambiguationData":[OSD([subQ4])]})])],"derivedFrom":makeQuery(id+"F5.opExtrude","CAP_FACE",FACE,{"disambiguationData":[OSD([subQ4,subQ6,subQ7,subQ5,subQ3,subQ2,subQ1,subQ0,sQuery(id+"F4.wireOp",EDGE,"E41"),sQuery(id+"F4.wireOp",EDGE,"E42"),sQuery(id+"F4.wireOp",EDGE,"E43"),sQuery(id+"F4.wireOp",EDGE,"E45"),sQuery(id+"F4.wireOp",EDGE,"E46"),sQuery(id+"F4.wireOp",EDGE,"E47.filletArc"),sQuery(id+"F4.wireOp",EDGE,"E48.filletArc"),sQuery(id+"F4.wireOp",EDGE,"E49.filletArc"),sQuery(id+"F4.wireOp",EDGE,"E50.filletArc"),sQuery(id+"F4.wireOp",EDGE,"E51.filletArc"),sQuery(id+"F4.wireOp",EDGE,"E52.filletArc"),sQuery(id+"F4.wireOp",EDGE,"E53.0.MirrorCS"),sQuery(id+"F4.wireOp",EDGE,"E54.0.MirrorCS"),sQuery(id+"F4.wireOp",EDGE,"E55.0.MirrorCS"),sQuery(id+"F4.wireOp",EDGE,"E56.0.MirrorCS"),sQuery(id+"F4.wireOp",EDGE,"E57.0.MirrorCS"),sQuery(id+"F4.wireOp",EDGE,"E58.0.MirrorCS"),sQuery(id+"F4.wireOp",EDGE,"E59.0.MirrorCS"),sQuery(id+"F4.wireOp",EDGE,"E60.0.MirrorCS"),sQuery(id+"F4.wireOp",EDGE,"E61.0.MirrorCS"),sQuery(id+"F4.wireOp",EDGE,"E62.0.MirrorCS"),sQuery(id+"F4.wireOp",EDGE,"E63.0.MirrorCS")])],"isStart":true})});}
            extrude(context, id + "F17", {"entities" : qUnion([Q0, Q1, Q2]), "endBound" : BoundingType.UP_TO_SURFACE, "endBoundEntityFace" : qUnion([Q3]), "depth" : 25 * mm});
        }
    });
